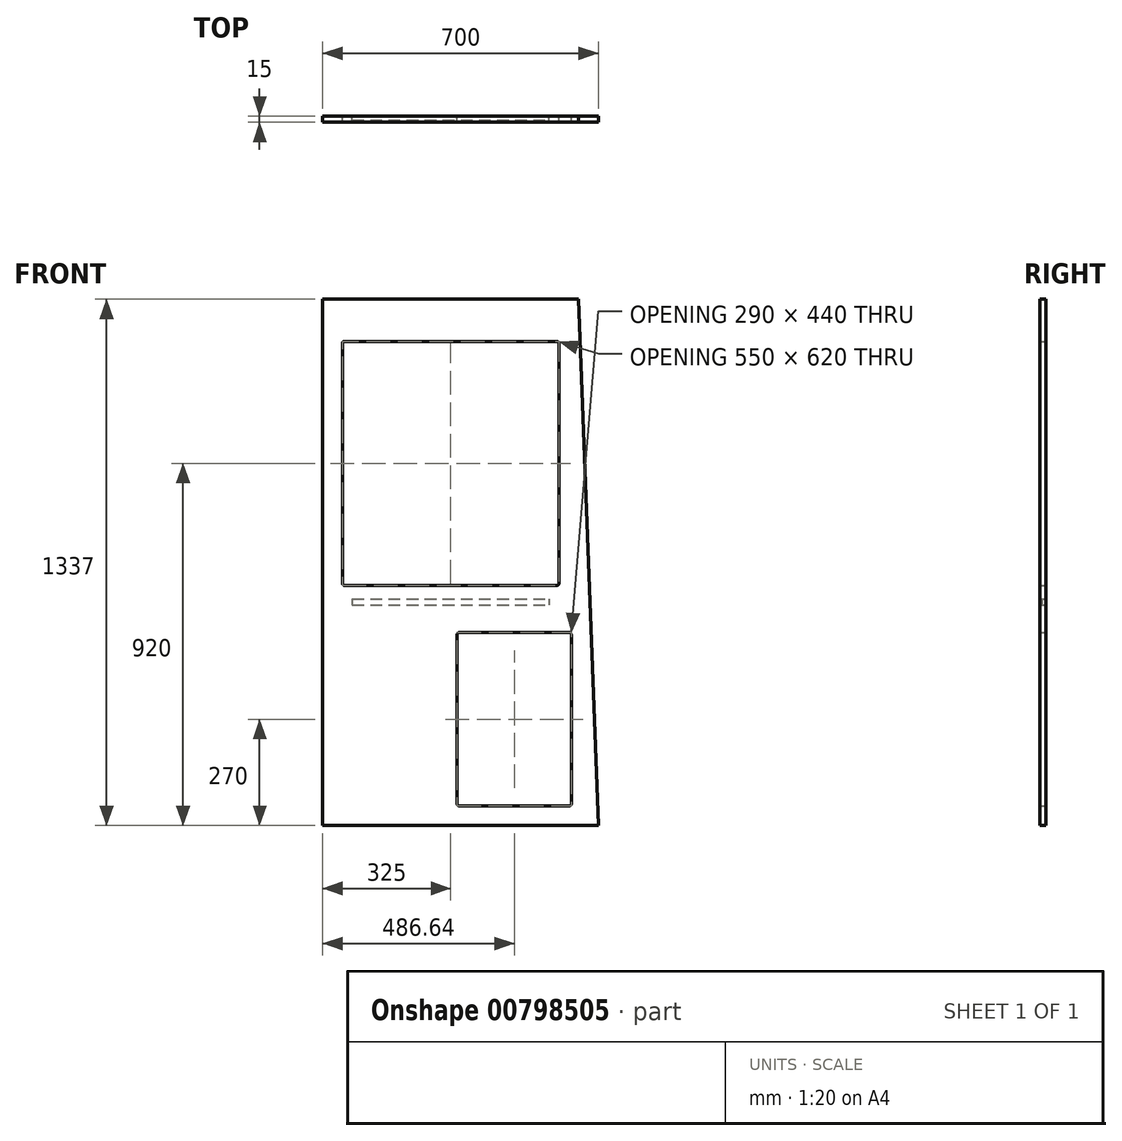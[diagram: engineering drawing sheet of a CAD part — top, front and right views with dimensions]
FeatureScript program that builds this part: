
annotation { "Feature Type Name" : "Feature", "Feature Type Description" : "" }
export const myFeature = defineFeature(function(context is Context, id is Id, definition is map)
    precondition{}
    {
        {
            var Q0;
            Q0=qCreatedBy(makeId("Front.planeOp"),FACE);
            var sketch = newSketch(context, id + "F0", { "sketchPlane" : qUnion([Q0])});
            skLineSegment(sketch, "E0", {"start": v(0, 0) * mm, "end": v(0, -1337) * mm});
            skLineSegment(sketch, "E1", {"start": v(0, 0) * mm, "end": v(650, 0) * mm});
            skLineSegment(sketch, "E2", {"start": v(650, 0) * mm, "end": v(700, -1337) * mm});
            skLineSegment(sketch, "E3", {"start": v(700, -1337) * mm, "end": v(0, -1337) * mm});
            skLineSegment(sketch, "E4.bottom", {"start": v(346.64, -847) * mm, "end": v(626.64, -847) * mm});
            skLineSegment(sketch, "E4.top", {"start": v(346.64, -1287) * mm, "end": v(626.64, -1287) * mm});
            skLineSegment(sketch, "E4.left", {"start": v(341.64, -852) * mm, "end": v(341.64, -1282) * mm});
            skLineSegment(sketch, "E4.right", {"start": v(631.64, -852) * mm, "end": v(631.64, -1282) * mm});
            skLineSegment(sketch, "E5.bottom", {"start": v(75, -762) * mm, "end": v(575, -762) * mm});
            skLineSegment(sketch, "E5.top", {"start": v(75, -777) * mm, "end": v(575, -777) * mm});
            skLineSegment(sketch, "E5.left", {"start": v(75, -762) * mm, "end": v(75, -777) * mm});
            skLineSegment(sketch, "E5.right", {"start": v(575, -762) * mm, "end": v(575, -777) * mm});
            skLineSegment(sketch, "E6.bottom", {"start": v(595, -107) * mm, "end": v(55, -107) * mm});
            skLineSegment(sketch, "E6.top", {"start": v(595, -727) * mm, "end": v(55, -727) * mm});
            skLineSegment(sketch, "E6.left", {"start": v(600, -112) * mm, "end": v(600, -722) * mm});
            skLineSegment(sketch, "E6.right", {"start": v(50, -112) * mm, "end": v(50, -722) * mm});
            skPoint(sketch, "E7.visualSharp", {"position": v(50, -107) * mm});
            skArc(sketch, "E7.filletArc", {"start": v(55, -107) * mm, "mid": v(51.46, -108.46) * mm, "end": v(50, -112) * mm});
            skPoint(sketch, "E8.visualSharp", {"position": v(600, -107) * mm});
            skArc(sketch, "E8.filletArc", {"start": v(600, -112) * mm, "mid": v(598.54, -108.46) * mm, "end": v(595, -107) * mm});
            skPoint(sketch, "E9.visualSharp", {"position": v(600, -727) * mm});
            skArc(sketch, "E9.filletArc", {"start": v(595, -727) * mm, "mid": v(598.54, -725.54) * mm, "end": v(600, -722) * mm});
            skPoint(sketch, "E10.visualSharp", {"position": v(50, -727) * mm});
            skArc(sketch, "E10.filletArc", {"start": v(50, -722) * mm, "mid": v(51.46, -725.54) * mm, "end": v(55, -727) * mm});
            skPoint(sketch, "E11.visualSharp", {"position": v(341.64, -847) * mm});
            skArc(sketch, "E11.filletArc", {"start": v(346.64, -847) * mm, "mid": v(343.1, -848.46) * mm, "end": v(341.64, -852) * mm});
            skPoint(sketch, "E12.visualSharp", {"position": v(631.64, -847) * mm});
            skArc(sketch, "E12.filletArc", {"start": v(631.64, -852) * mm, "mid": v(630.18, -848.46) * mm, "end": v(626.64, -847) * mm});
            skPoint(sketch, "E13.visualSharp", {"position": v(341.64, -1287) * mm});
            skArc(sketch, "E13.filletArc", {"start": v(341.64, -1282) * mm, "mid": v(343.1, -1285.54) * mm, "end": v(346.64, -1287) * mm});
            skPoint(sketch, "E14.visualSharp", {"position": v(631.64, -1287) * mm});
            skArc(sketch, "E14.filletArc", {"start": v(626.64, -1287) * mm, "mid": v(630.18, -1285.54) * mm, "end": v(631.64, -1282) * mm});
            skSolve(sketch);
        }
        {
            var Q0;
            Q0=makeQuery(id+"F0.imprint","IMPRINT",FACE,{"disambiguationData":[TD([[makeQuery(id+"F0.imprint","IMPRINT",EDGE,{"derivedFrom":sQuery(id+"F0.wireOp",EDGE,"E0")}),1.0]])]});
            var Q1;
            Q1=makeQuery(id+"F0.imprint","IMPRINT",FACE,{"disambiguationData":[TD([[makeQuery(id+"F0.imprint","IMPRINT",EDGE,{"derivedFrom":sQuery(id+"F0.wireOp",EDGE,"E5.bottom")}),-1.0]])]});
            extrude(context, id + "F1", {"entities" : qUnion([Q0, Q1]), "depth" : 15 * mm, "offsetDistance" : 25 * mm});
        }
        {
            var Q0;
            Q0=makeQuery(id+"F0.imprint","IMPRINT",FACE,{"disambiguationData":[TD([[makeQuery(id+"F0.imprint","IMPRINT",EDGE,{"derivedFrom":sQuery(id+"F0.wireOp",EDGE,"E5.bottom")}),-1.0]])]});
            extrude(context, id + "F2", {"entities" : qUnion([Q0]), "operationType" : NewBodyOperationType.REMOVE, "depth" : 10 * mm, "offsetDistance" : 25 * mm});
        }
    });
